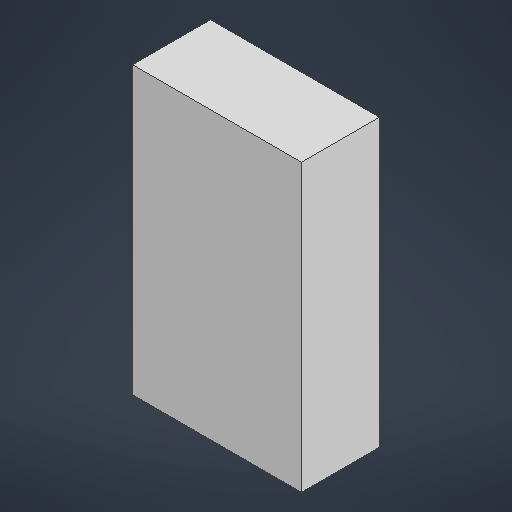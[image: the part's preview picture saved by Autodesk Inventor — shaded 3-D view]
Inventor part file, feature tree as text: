
AUTODESK INVENTOR PART (.ipt)
format: ipt  version: 2025.3 (Build 293356000, 356)  size: 155,136 bytes
history: native  units: mm
features: extrude x1, sketch x1
ambient origin geometry x8: Origin, YZ Plane, XZ Plane, XY Plane, X Axis, Y Axis, Z Axis, Center Point
bodies: Solid1 (feature_tree)
feature tree (2):
  extrude  "Extrusion1"  Depth=6.0mm
  sketch  "Sketch1"  dims[d0=13.0mm d1=6.0mm d2=22.0mm d3=0.0mm]
